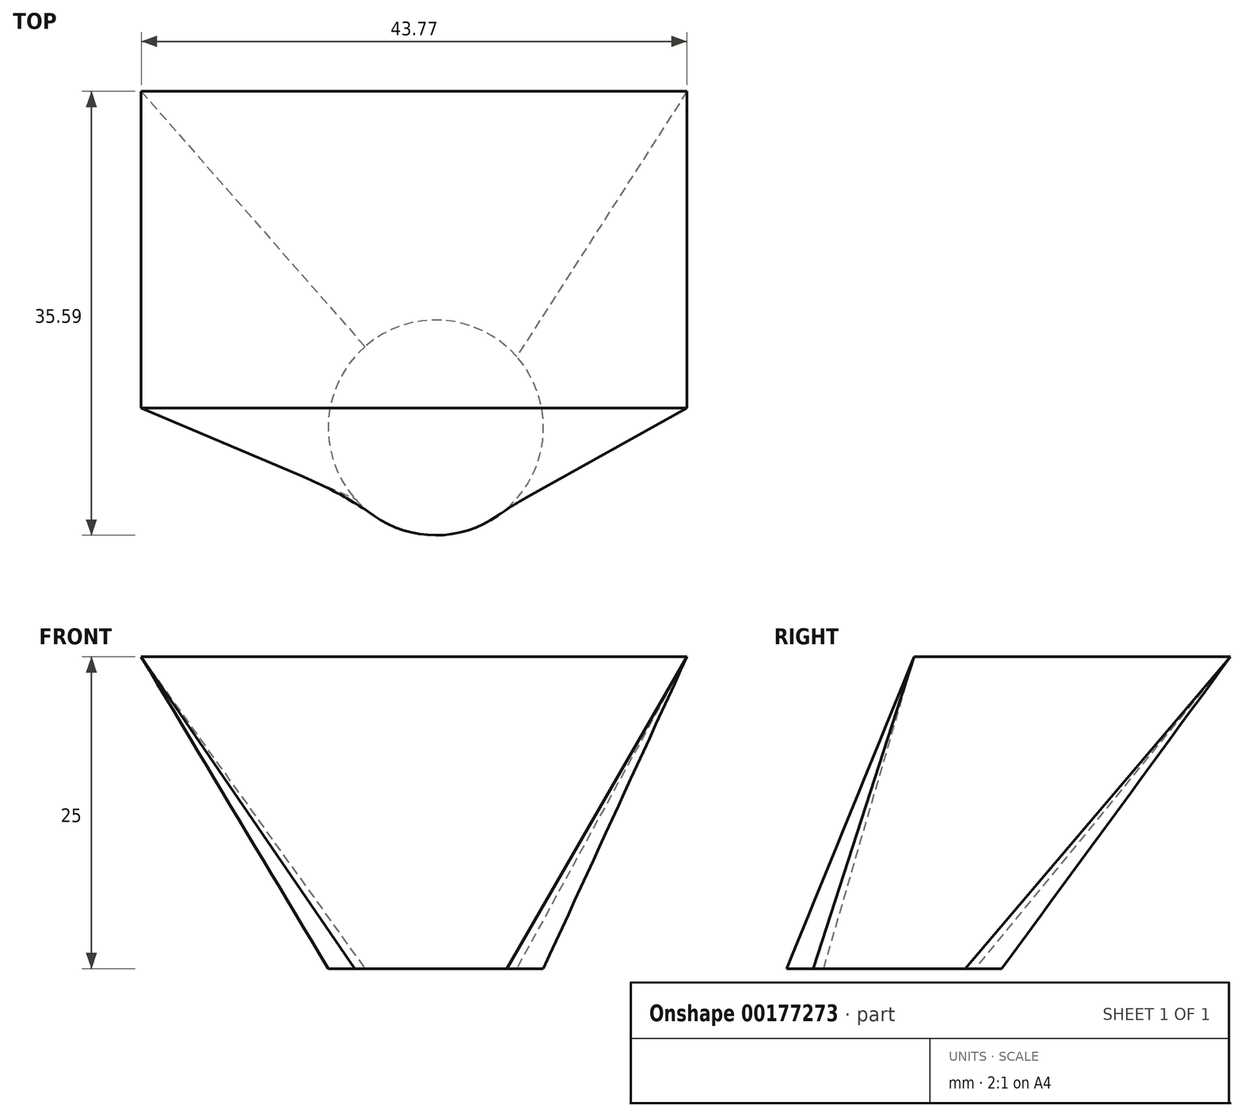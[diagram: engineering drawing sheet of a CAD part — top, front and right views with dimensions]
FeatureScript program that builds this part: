
annotation { "Feature Type Name" : "Feature", "Feature Type Description" : "" }
export const myFeature = defineFeature(function(context is Context, id is Id, definition is map)
    precondition{}
    {
        {
            var Q0;
            Q0=qCreatedBy(makeId("Top.planeOp"),FACE);
            var sketch = newSketch(context, id + "F0", { "sketchPlane" : qUnion([Q0])});
            skCircle(sketch, "E0", {"center": v(-32.91, 10.86) * mm, "radius": 8.63 * mm});
            skCircle(sketch, "E1", {"center": v(-32.91, 10.86) * mm, "radius": 10.65 * mm});
            skSolve(sketch);
        }
        {
            var Q0;
            Q0=qCreatedBy(makeId("Top.planeOp"),FACE);
            cPlane(context, id + "F1", {"entities" : qUnion([Q0]), "cplaneType" : CPlaneType.OFFSET, "offset" : 25 * mm, "width" : 150 * mm, "height" : 150 * mm});
        }
        {
            var Q0;
            Q0=qCreatedBy(id+"F1.planeOp",FACE);
            var sketch = newSketch(context, id + "F2", { "sketchPlane" : qUnion([Q0])});
            skLineSegment(sketch, "E2.bottom", {"start": v(-56.54, 37.83) * mm, "end": v(-12.77, 37.83) * mm});
            skLineSegment(sketch, "E2.top", {"start": v(-56.54, 12.45) * mm, "end": v(-12.77, 12.45) * mm});
            skLineSegment(sketch, "E2.left", {"start": v(-56.54, 37.83) * mm, "end": v(-56.54, 12.45) * mm});
            skLineSegment(sketch, "E2.right", {"start": v(-12.77, 37.83) * mm, "end": v(-12.77, 12.45) * mm});
            skLineSegment(sketch, "E3.bottom", {"start": v(-60.5, 41.95) * mm, "end": v(-9.6, 41.95) * mm});
            skLineSegment(sketch, "E3.top", {"start": v(-60.5, 9.91) * mm, "end": v(-9.6, 9.91) * mm});
            skLineSegment(sketch, "E3.left", {"start": v(-60.5, 41.95) * mm, "end": v(-60.5, 9.91) * mm});
            skLineSegment(sketch, "E3.right", {"start": v(-9.6, 41.95) * mm, "end": v(-9.6, 9.91) * mm});
            skSolve(sketch);
        }
        {
            var Q0;
            Q0=makeQuery(id+"F2.imprint","IMPRINT",FACE,{"disambiguationData":[TD([[makeQuery(id+"F2.imprint","IMPRINT",EDGE,{"derivedFrom":sQuery(id+"F2.wireOp",EDGE,"E2.bottom")}),-1.0]])]});
            var Q1;
            Q1=makeQuery(id+"F0.imprint","IMPRINT",FACE,{"disambiguationData":[TD([[makeQuery(id+"F0.imprint","IMPRINT",EDGE,{"derivedFrom":sQuery(id+"F0.wireOp",EDGE,"E0")}),1.0]])]});
            loft(context, id + "F3", {"sheetProfilesArray" : [{ "sheetProfileEntities" : qUnion([Q0]) }, { "sheetProfileEntities" : qUnion([Q1]) }]});
        }
    });
